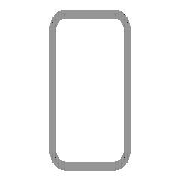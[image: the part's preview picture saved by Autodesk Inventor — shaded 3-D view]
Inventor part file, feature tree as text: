
AUTODESK INVENTOR PART (.ipt)
format: ipt  version: 2025 (Build 290162010, 162A)  size: 135,168 bytes
history: native  units: mm (DEFAULTED — no unit token found)
features: other x4, sketch x1, plane x1
ambient origin geometry x8: Origin, YZ Plane, XZ Plane, XY Plane, X Axis, Y Axis, Z Axis, Center Point
bodies: Solid1 (feature_tree), Body (feature_tree)
feature tree (6):
  parser-record x1  (decoder bookkeeping rows leaked as tree rows — omitted from the tree; the rows remain in map.json)
  other  "Driven Length"
  other  "Start Plane"
  other  "End Plane"
  sketch  "Sketch3"  dims[d3=1500.0mm d4=0.0mm d7=6.0mm d9=40.0mm d11=60.0mm d12=3.0mm d13=-0.0mm d14=1500.0mm d15=20.0mm d16=30.0mm d17=90.0deg d18=1500.0mm]
  plane  "Work Plane3"
